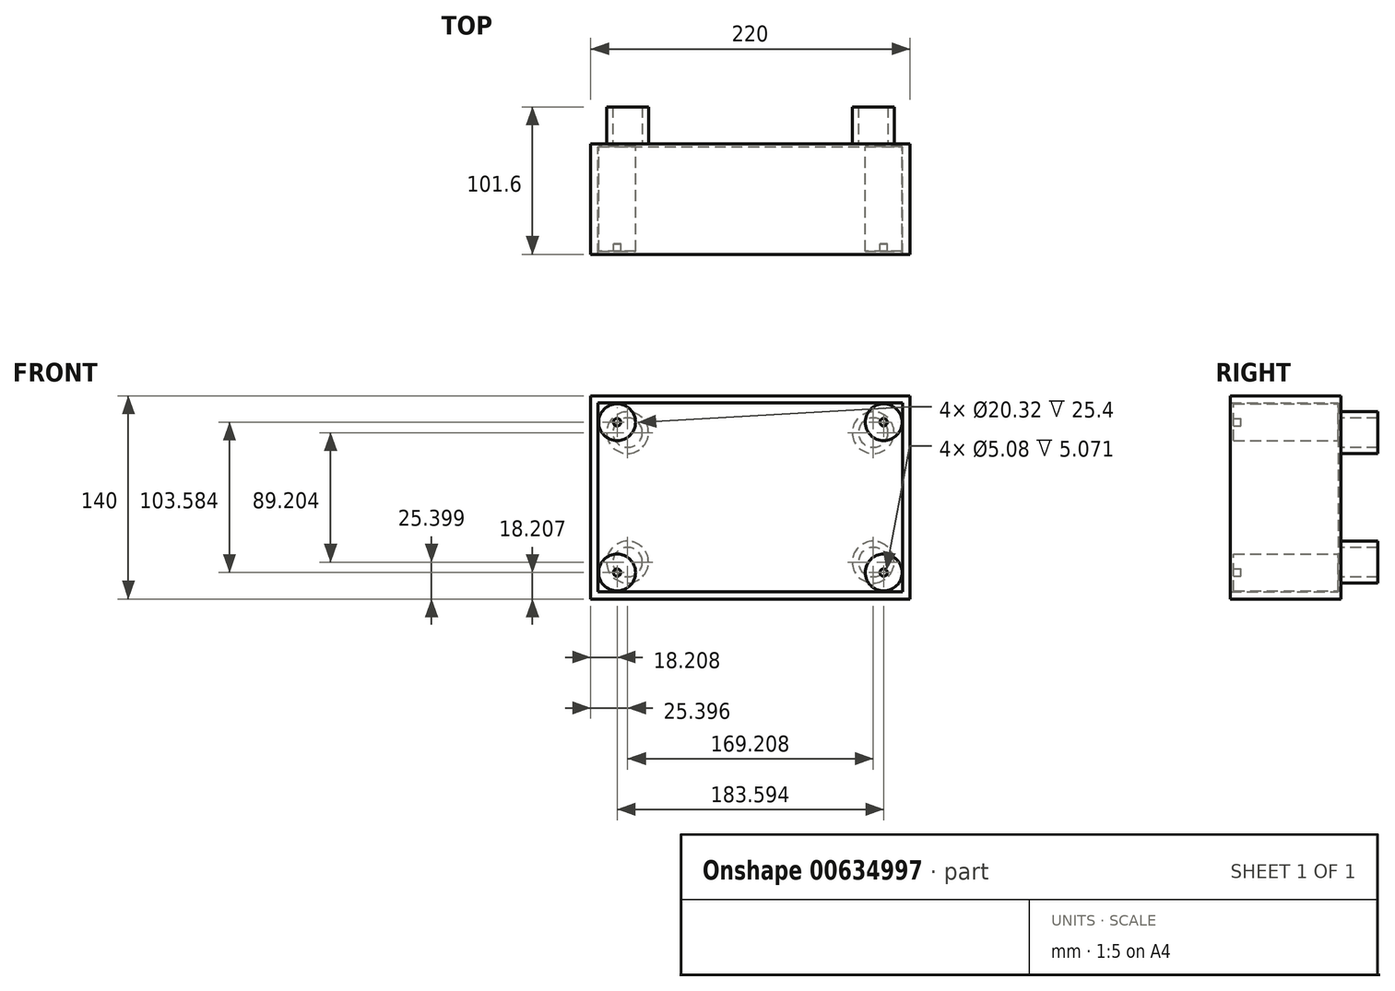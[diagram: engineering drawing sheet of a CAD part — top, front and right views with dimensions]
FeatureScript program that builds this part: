
annotation { "Feature Type Name" : "Feature", "Feature Type Description" : "" }
export const myFeature = defineFeature(function(context is Context, id is Id, definition is map)
    precondition{}
    {
        {
            var Q0;
            Q0=qCreatedBy(makeId("Front.planeOp"),FACE);
            var sketch = newSketch(context, id + "F0", { "sketchPlane" : qUnion([Q0])});
            skLineSegment(sketch, "E0.bottom", {"start": v(-111.04, 60.4) * mm, "end": v(98.96, 60.4) * mm});
            skLineSegment(sketch, "E0.top", {"start": v(-111.04, -69.6) * mm, "end": v(98.96, -69.6) * mm});
            skLineSegment(sketch, "E0.left", {"start": v(-111.04, 60.4) * mm, "end": v(-111.04, -69.6) * mm});
            skLineSegment(sketch, "E0.right", {"start": v(98.96, 60.4) * mm, "end": v(98.96, -69.6) * mm});
            skLineSegment(sketch, "E1", {"start": v(-111.06, 65.4) * mm, "end": v(-0.24, 65.4) * mm});
            skLineSegment(sketch, "E2", {"start": v(-116.04, 60.4) * mm, "end": v(-116.04, 0) * mm});
            skLineSegment(sketch, "E3", {"start": v(-111.06, 65.4) * mm, "end": v(-116.04, 65.4) * mm});
            skLineSegment(sketch, "E4", {"start": v(-116.04, 65.4) * mm, "end": v(-116.04, 60.4) * mm});
            skPoint(sketch, "E5.start.orphan", {"position": v(0, 60.4) * mm});
            skLineSegment(sketch, "E6", {"start": v(-0.24, 65.4) * mm, "end": v(98.94, 65.4) * mm});
            skLineSegment(sketch, "E7", {"start": v(98.94, 65.4) * mm, "end": v(103.96, 65.4) * mm});
            skLineSegment(sketch, "E8", {"start": v(103.96, 65.4) * mm, "end": v(103.96, 60.4) * mm});
            skLineSegment(sketch, "E9", {"start": v(103.96, 60.4) * mm, "end": v(103.96, -69.6) * mm});
            skLineSegment(sketch, "E10", {"start": v(-116.04, 0) * mm, "end": v(-116.04, -69.6) * mm});
            skLineSegment(sketch, "E11", {"start": v(-111.04, -74.6) * mm, "end": v(98.96, -74.6) * mm});
            skLineSegment(sketch, "E12", {"start": v(-111.04, -74.6) * mm, "end": v(-116.04, -74.6) * mm});
            skLineSegment(sketch, "E13", {"start": v(-116.04, -74.6) * mm, "end": v(-116.04, -69.6) * mm});
            skLineSegment(sketch, "E14", {"start": v(103.96, -74.6) * mm, "end": v(98.96, -74.6) * mm});
            skLineSegment(sketch, "E15", {"start": v(103.96, -74.6) * mm, "end": v(103.96, -69.6) * mm});
            skSolve(sketch);
        }
        {
            var Q0;
            Q0=makeQuery(id+"F0.imprint","IMPRINT",FACE,{"disambiguationData":[TD([[makeQuery(id+"F0.imprint","IMPRINT",EDGE,{"derivedFrom":sQuery(id+"F0.wireOp",EDGE,"E0.bottom")}),-1.0]])]});
            extrude(context, id + "F1", {"entities" : qUnion([Q0]), "depth" : 2 * mm, "offsetDistance" : 25.4 * mm});
        }
        {
            var Q0;
            Q0 = qSketchRegion(id + "F0", true);
            extrude(context, id + "F2", {"entities" : qUnion([Q0]), "operationType" : NewBodyOperationType.ADD, "depth" : 76.2 * mm, "offsetDistance" : 25.4 * mm});
        }
        {
            var Q0;
            {var subQ0=sQuery(id+"F0.wireOp",EDGE,"E0.right");var subQ1=sQuery(id+"F0.wireOp",EDGE,"E0.left");var subQ2=sQuery(id+"F0.wireOp",EDGE,"E0.top");var subQ3=sQuery(id+"F0.wireOp",EDGE,"E0.bottom");Q0=makeQuery(id+"F2.boolean.opBoolean","MERGE",FACE,{"derivedFrom":[makeQuery(id+"F1.opExtrude","CAP_FACE",FACE,{"disambiguationData":[OSD([subQ3,subQ2,subQ1,subQ0])],"isStart":true}),makeQuery(id+"F2.opExtrude","CAP_FACE",FACE,{"disambiguationData":[OSD([subQ3,subQ2,subQ1,subQ0,sQuery(id+"F0.wireOp",EDGE,"E1"),sQuery(id+"F0.wireOp",EDGE,"E2"),sQuery(id+"F0.wireOp",EDGE,"E3"),sQuery(id+"F0.wireOp",EDGE,"E4"),sQuery(id+"F0.wireOp",EDGE,"E6"),sQuery(id+"F0.wireOp",EDGE,"E7"),sQuery(id+"F0.wireOp",EDGE,"E8"),sQuery(id+"F0.wireOp",EDGE,"E9"),sQuery(id+"F0.wireOp",EDGE,"E10"),sQuery(id+"F0.wireOp",EDGE,"E11"),sQuery(id+"F0.wireOp",EDGE,"E12"),sQuery(id+"F0.wireOp",EDGE,"E13"),sQuery(id+"F0.wireOp",EDGE,"E14"),sQuery(id+"F0.wireOp",EDGE,"E15")])],"isStart":true})]});}
            var sketch = newSketch(context, id + "F3", { "sketchPlane" : qUnion([Q0])});
            skCircle(sketch, "E16", {"center": v(-78.56, 40) * mm, "radius": 14.4 * mm});
            skLineSegment(sketch, "E17.bottom", {"start": v(116.04, 65.4) * mm, "end": v(90.64, 65.4) * mm});
            skLineSegment(sketch, "E17.top", {"start": v(116.04, 40) * mm, "end": v(100.8, 40) * mm});
            skLineSegment(sketch, "E17.left", {"start": v(116.04, 65.4) * mm, "end": v(116.04, 40) * mm});
            skLineSegment(sketch, "E17.right", {"start": v(90.64, 65.4) * mm, "end": v(90.64, 50.16) * mm});
            skCircle(sketch, "E18", {"center": v(90.64, 40) * mm, "radius": 14.4 * mm});
            skLineSegment(sketch, "E19.bottom", {"start": v(-103.96, -74.6) * mm, "end": v(-78.56, -74.6) * mm});
            skLineSegment(sketch, "E19.top", {"start": v(-103.96, -49.2) * mm, "end": v(-88.72, -49.2) * mm});
            skLineSegment(sketch, "E19.left", {"start": v(-103.96, -74.6) * mm, "end": v(-103.96, -49.2) * mm});
            skLineSegment(sketch, "E19.right", {"start": v(-78.56, -74.6) * mm, "end": v(-78.56, -59.36) * mm});
            skLineSegment(sketch, "E20.bottom", {"start": v(-103.96, 65.4) * mm, "end": v(-78.56, 65.4) * mm});
            skLineSegment(sketch, "E20.top", {"start": v(-103.96, 40) * mm, "end": v(-88.72, 40) * mm});
            skLineSegment(sketch, "E20.left", {"start": v(-103.96, 65.4) * mm, "end": v(-103.96, 40) * mm});
            skLineSegment(sketch, "E20.right", {"start": v(-78.56, 65.4) * mm, "end": v(-78.56, 50.16) * mm});
            skCircle(sketch, "E21", {"center": v(-78.56, -49.2) * mm, "radius": 14.4 * mm});
            skLineSegment(sketch, "E22.bottom", {"start": v(116.04, -74.6) * mm, "end": v(90.64, -74.6) * mm});
            skLineSegment(sketch, "E22.top", {"start": v(116.04, -49.2) * mm, "end": v(100.8, -49.2) * mm});
            skLineSegment(sketch, "E22.left", {"start": v(116.04, -74.6) * mm, "end": v(116.04, -49.2) * mm});
            skLineSegment(sketch, "E22.right", {"start": v(90.64, -74.6) * mm, "end": v(90.64, -49.2) * mm});
            skCircle(sketch, "E23", {"center": v(90.64, -49.2) * mm, "radius": 14.4 * mm});
            skCircle(sketch, "E24", {"center": v(-78.56, 40) * mm, "radius": 10.16 * mm});
            skCircle(sketch, "E25", {"center": v(90.64, 40) * mm, "radius": 10.16 * mm});
            skCircle(sketch, "E26", {"center": v(-78.56, -49.2) * mm, "radius": 10.16 * mm});
            skCircle(sketch, "E27", {"center": v(90.64, -49.2) * mm, "radius": 10.16 * mm});
            skSolve(sketch);
        }
        {
            var Q0;
            {var subQ0=sQuery(id+"F3.wireOp",EDGE,"E20.top");var subQ1=sQuery(id+"F3.wireOp",EDGE,"E16");var subQ2=makeQuery(id+"F3.imprint","INTERSECT",VERTEX,{"derivedFrom":[subQ1,subQ0]});Q0=makeQuery(id+"F3.imprint","IMPRINT",FACE,{"disambiguationData":[TD([[makeQuery(id+"F3.imprint","IMPRINT",EDGE,{"disambiguationData":[TD([[subQ2,-1.0]])],"derivedFrom":subQ1}),1.0]])]});}
            var Q1;
            {var subQ0=sQuery(id+"F3.wireOp",EDGE,"E20.top");var subQ1=sQuery(id+"F3.wireOp",EDGE,"E16");var subQ2=makeQuery(id+"F3.imprint","INTERSECT",VERTEX,{"derivedFrom":[subQ1,subQ0]});Q1=makeQuery(id+"F3.imprint","IMPRINT",FACE,{"disambiguationData":[TD([[makeQuery(id+"F3.imprint","IMPRINT",EDGE,{"disambiguationData":[TD([[subQ2,1.0]])],"derivedFrom":subQ1}),1.0]])]});}
            var Q2;
            {var subQ0=sQuery(id+"F3.wireOp",EDGE,"E21");var subQ1=sQuery(id+"F3.wireOp",EDGE,"E19.top");var subQ2=makeQuery(id+"F3.imprint","INTERSECT",VERTEX,{"derivedFrom":[subQ1,subQ0]});Q2=makeQuery(id+"F3.imprint","IMPRINT",FACE,{"disambiguationData":[TD([[makeQuery(id+"F3.imprint","IMPRINT",EDGE,{"disambiguationData":[TD([[subQ2,-1.0]])],"derivedFrom":subQ1}),1.0]])]});}
            var Q3;
            {var subQ0=sQuery(id+"F3.wireOp",EDGE,"E21");var subQ1=sQuery(id+"F3.wireOp",EDGE,"E19.top");var subQ2=makeQuery(id+"F3.imprint","INTERSECT",VERTEX,{"derivedFrom":[subQ1,subQ0]});Q3=makeQuery(id+"F3.imprint","IMPRINT",FACE,{"disambiguationData":[TD([[makeQuery(id+"F3.imprint","IMPRINT",EDGE,{"disambiguationData":[TD([[subQ2,-1.0]])],"derivedFrom":subQ1}),-1.0]])]});}
            var Q4;
            {var subQ0=sQuery(id+"F3.wireOp",EDGE,"E18");var subQ1=sQuery(id+"F3.wireOp",EDGE,"E17.top");var subQ2=makeQuery(id+"F3.imprint","INTERSECT",VERTEX,{"derivedFrom":[subQ1,subQ0]});Q4=makeQuery(id+"F3.imprint","IMPRINT",FACE,{"disambiguationData":[TD([[makeQuery(id+"F3.imprint","IMPRINT",EDGE,{"disambiguationData":[TD([[subQ2,-1.0]])],"derivedFrom":subQ1}),-1.0]])]});}
            var Q5;
            {var subQ0=sQuery(id+"F3.wireOp",EDGE,"E18");var subQ1=sQuery(id+"F3.wireOp",EDGE,"E17.top");var subQ2=makeQuery(id+"F3.imprint","INTERSECT",VERTEX,{"derivedFrom":[subQ1,subQ0]});Q5=makeQuery(id+"F3.imprint","IMPRINT",FACE,{"disambiguationData":[TD([[makeQuery(id+"F3.imprint","IMPRINT",EDGE,{"disambiguationData":[TD([[subQ2,-1.0]])],"derivedFrom":subQ1}),1.0]])]});}
            var Q6;
            {var subQ0=sQuery(id+"F3.wireOp",EDGE,"E23");var subQ1=sQuery(id+"F3.wireOp",EDGE,"E22.top");var subQ2=makeQuery(id+"F3.imprint","INTERSECT",VERTEX,{"derivedFrom":[subQ1,subQ0]});Q6=makeQuery(id+"F3.imprint","IMPRINT",FACE,{"disambiguationData":[TD([[makeQuery(id+"F3.imprint","IMPRINT",EDGE,{"disambiguationData":[TD([[subQ2,-1.0]])],"derivedFrom":subQ1}),-1.0]])]});}
            var Q7;
            {var subQ0=sQuery(id+"F3.wireOp",EDGE,"E23");var subQ1=sQuery(id+"F3.wireOp",EDGE,"E22.top");var subQ2=makeQuery(id+"F3.imprint","INTERSECT",VERTEX,{"derivedFrom":[subQ1,subQ0]});Q7=makeQuery(id+"F3.imprint","IMPRINT",FACE,{"disambiguationData":[TD([[makeQuery(id+"F3.imprint","IMPRINT",EDGE,{"disambiguationData":[TD([[subQ2,-1.0]])],"derivedFrom":subQ1}),1.0]])]});}
            extrude(context, id + "F4", {"entities" : qUnion([Q0, Q1, Q2, Q3, Q4, Q5, Q6, Q7]), "operationType" : NewBodyOperationType.ADD, "depth" : 25.4 * mm, "offsetDistance" : 25.4 * mm});
        }
        {
            var Q0;
            Q0=makeQuery(id+"F1.opExtrude","CAP_FACE",FACE,{"disambiguationData":[OSD([sQuery(id+"F0.wireOp",EDGE,"E0.bottom"),sQuery(id+"F0.wireOp",EDGE,"E0.top"),sQuery(id+"F0.wireOp",EDGE,"E0.left"),sQuery(id+"F0.wireOp",EDGE,"E0.right")])],"isStart":false});
            var sketch = newSketch(context, id + "F5", { "sketchPlane" : qUnion([Q0])});
            skLineSegment(sketch, "E28.bottom", {"start": v(98.96, -69.6) * mm, "end": v(85.76, -69.6) * mm});
            skLineSegment(sketch, "E28.top", {"start": v(98.96, -56.4) * mm, "end": v(98.46, -56.4) * mm});
            skLineSegment(sketch, "E28.left", {"start": v(98.96, -69.6) * mm, "end": v(98.96, -56.4) * mm});
            skLineSegment(sketch, "E28.right", {"start": v(85.76, -69.6) * mm, "end": v(85.76, -69.1) * mm});
            skCircle(sketch, "E29", {"center": v(85.76, -56.4) * mm, "radius": 12.7 * mm});
            skLineSegment(sketch, "E30", {"start": v(-111.04, -69.6) * mm, "end": v(-97.83, -69.6) * mm});
            skLineSegment(sketch, "E31", {"start": v(-111.04, -69.6) * mm, "end": v(-111.04, -56.4) * mm});
            skLineSegment(sketch, "E32", {"start": v(-97.83, -69.6) * mm, "end": v(-97.83, -69.1) * mm});
            skLineSegment(sketch, "E33", {"start": v(-110.53, -56.4) * mm, "end": v(-111.04, -56.4) * mm});
            skCircle(sketch, "E34", {"center": v(-97.83, -56.4) * mm, "radius": 12.7 * mm});
            skLineSegment(sketch, "E35.bottom", {"start": v(98.96, 60.4) * mm, "end": v(85.75, 60.4) * mm});
            skLineSegment(sketch, "E35.top", {"start": v(98.96, 47.2) * mm, "end": v(98.45, 47.2) * mm});
            skLineSegment(sketch, "E35.left", {"start": v(98.96, 60.4) * mm, "end": v(98.96, 47.2) * mm});
            skLineSegment(sketch, "E35.right", {"start": v(85.75, 60.4) * mm, "end": v(85.75, 59.9) * mm});
            skLineSegment(sketch, "E36.bottom", {"start": v(-111.04, 60.4) * mm, "end": v(-97.83, 60.4) * mm});
            skLineSegment(sketch, "E36.top", {"start": v(-111.04, 47.2) * mm, "end": v(-110.53, 47.2) * mm});
            skLineSegment(sketch, "E36.left", {"start": v(-111.04, 60.4) * mm, "end": v(-111.04, 47.2) * mm});
            skLineSegment(sketch, "E36.right", {"start": v(-97.83, 60.4) * mm, "end": v(-97.83, 59.9) * mm});
            skCircle(sketch, "E37", {"center": v(85.75, 47.2) * mm, "radius": 12.7 * mm});
            skCircle(sketch, "E38", {"center": v(-97.83, 47.2) * mm, "radius": 12.7 * mm});
            skCircle(sketch, "E39", {"center": v(-97.83, 47.2) * mm, "radius": 2.54 * mm});
            skCircle(sketch, "E40", {"center": v(85.75, 47.2) * mm, "radius": 2.54 * mm});
            skCircle(sketch, "E41", {"center": v(85.76, -56.4) * mm, "radius": 2.54 * mm});
            skCircle(sketch, "E42", {"center": v(-97.83, -56.4) * mm, "radius": 2.54 * mm});
            skLineSegment(sketch, "E43", {"start": v(-85.13, 60.4) * mm, "end": v(-85.13, 64.87) * mm});
            skLineSegment(sketch, "E44", {"start": v(73.05, 60.4) * mm, "end": v(73.05, 65.4) * mm});
            skPoint(sketch, "E45.start.orphan", {"position": v(73.8, 65.4) * mm});
            skLineSegment(sketch, "E46", {"start": v(73.05, 65.4) * mm, "end": v(73.05, 60.4) * mm});
            skPoint(sketch, "E47.orphan", {"position": v(73.05, 47.2) * mm});
            skSolve(sketch);
        }
        {
            var Q0;
            {var subQ0=sQuery(id+"F5.wireOp",EDGE,"E29");var subQ1=makeQuery(id+"F5.imprint","INTERSECT",VERTEX,{"derivedFrom":[sQuery(id+"F5.wireOp",EDGE,"E28.top"),subQ0]});Q0=makeQuery(id+"F5.imprint","IMPRINT",FACE,{"disambiguationData":[TD([[makeQuery(id+"F5.imprint","IMPRINT",EDGE,{"disambiguationData":[TD([[subQ1,-1.0]])],"derivedFrom":subQ0}),1.0]])]});}
            var Q1;
            {var subQ0=sQuery(id+"F5.wireOp",EDGE,"E34");var subQ1=makeQuery(id+"F5.imprint","INTERSECT",VERTEX,{"derivedFrom":[sQuery(id+"F5.wireOp",EDGE,"E32"),subQ0]});Q1=makeQuery(id+"F5.imprint","IMPRINT",FACE,{"disambiguationData":[TD([[makeQuery(id+"F5.imprint","IMPRINT",EDGE,{"disambiguationData":[TD([[subQ1,1.0]])],"derivedFrom":subQ0}),1.0]])]});}
            var Q2;
            {var subQ0=sQuery(id+"F5.wireOp",EDGE,"E38");var subQ1=makeQuery(id+"F5.imprint","INTERSECT",VERTEX,{"derivedFrom":[sQuery(id+"F5.wireOp",EDGE,"E36.top"),subQ0]});Q2=makeQuery(id+"F5.imprint","IMPRINT",FACE,{"disambiguationData":[TD([[makeQuery(id+"F5.imprint","IMPRINT",EDGE,{"disambiguationData":[TD([[subQ1,1.0]])],"derivedFrom":subQ0}),1.0]])]});}
            var Q3;
            {var subQ0=sQuery(id+"F5.wireOp",EDGE,"E37");var subQ1=makeQuery(id+"F5.imprint","INTERSECT",VERTEX,{"derivedFrom":[sQuery(id+"F5.wireOp",EDGE,"E35.top"),subQ0]});Q3=makeQuery(id+"F5.imprint","IMPRINT",FACE,{"disambiguationData":[TD([[makeQuery(id+"F5.imprint","IMPRINT",EDGE,{"disambiguationData":[TD([[subQ1,-1.0]])],"derivedFrom":subQ0}),1.0]])]});}
            extrude(context, id + "F6", {"entities" : qUnion([Q0, Q1, Q2, Q3]), "operationType" : NewBodyOperationType.ADD, "depth" : 72 * mm, "offsetDistance" : 25.4 * mm});
        }
        {
            var Q0;
            Q0=makeQuery(id+"F5.imprint","IMPRINT",FACE,{"disambiguationData":[TD([[makeQuery(id+"F5.imprint","IMPRINT",EDGE,{"derivedFrom":sQuery(id+"F5.wireOp",EDGE,"E42")}),1.0]])]});
            var Q1;
            Q1=makeQuery(id+"F5.imprint","IMPRINT",FACE,{"disambiguationData":[TD([[makeQuery(id+"F5.imprint","IMPRINT",EDGE,{"derivedFrom":sQuery(id+"F5.wireOp",EDGE,"E41")}),1.0]])]});
            var Q2;
            Q2=makeQuery(id+"F5.imprint","IMPRINT",FACE,{"disambiguationData":[TD([[makeQuery(id+"F5.imprint","IMPRINT",EDGE,{"derivedFrom":sQuery(id+"F5.wireOp",EDGE,"E39")}),1.0]])]});
            var Q3;
            Q3=makeQuery(id+"F5.imprint","IMPRINT",FACE,{"disambiguationData":[TD([[makeQuery(id+"F5.imprint","IMPRINT",EDGE,{"derivedFrom":sQuery(id+"F5.wireOp",EDGE,"E40")}),1.0]])]});
            extrude(context, id + "F7", {"entities" : qUnion([Q0, Q1, Q2, Q3]), "operationType" : NewBodyOperationType.ADD, "depth" : 66.93 * mm, "offsetDistance" : 25.4 * mm});
        }
    });
